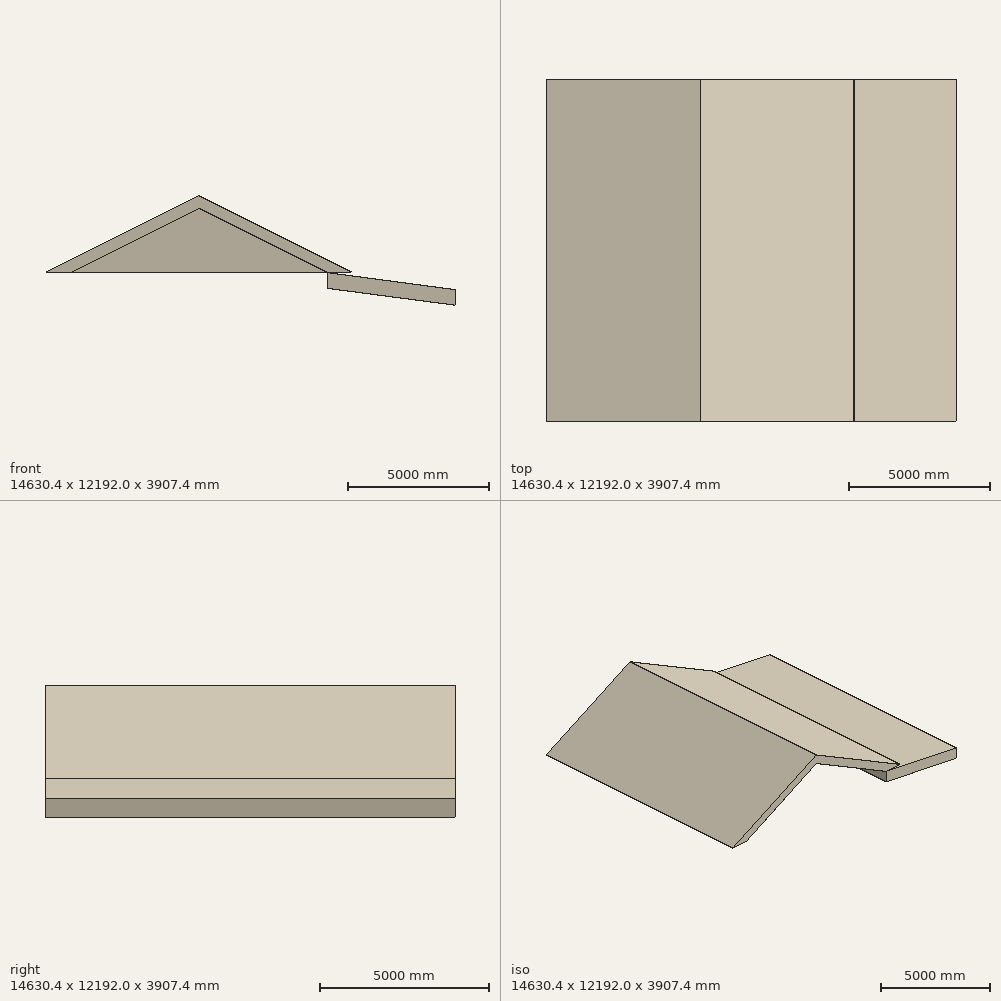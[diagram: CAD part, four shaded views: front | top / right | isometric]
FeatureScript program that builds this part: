
annotation { "Feature Type Name" : "Feature", "Feature Type Description" : "" }
export const myFeature = defineFeature(function(context is Context, id is Id, definition is map)
    precondition{}
    {
        {
            var Q0;
            Q0=qCreatedBy(makeId("Front.planeOp"),FACE);
            var sketch = newSketch(context, id + "F0", { "sketchPlane" : qUnion([Q0])});
            skLineSegment(sketch, "E0", {"start": v(0, 0) * mm, "end": v(-4572, 0) * mm});
            skLineSegment(sketch, "E1", {"start": v(0, 0) * mm, "end": v(4572, 0) * mm});
            skLineSegment(sketch, "E2", {"start": v(0, 0) * mm, "end": v(0, 2286) * mm});
            skLineSegment(sketch, "E3", {"start": v(0, 2286) * mm, "end": v(0, 2743.2) * mm});
            skLineSegment(sketch, "E4", {"start": v(4572, 0) * mm, "end": v(0, 2286) * mm});
            skLineSegment(sketch, "E5", {"start": v(0, 2286) * mm, "end": v(-4572, 0) * mm});
            skLineSegment(sketch, "E6", {"start": v(-4572, 0) * mm, "end": v(-5486.4, 0) * mm});
            skLineSegment(sketch, "E7", {"start": v(4572, 0) * mm, "end": v(5486.4, 0) * mm});
            skLineSegment(sketch, "E8", {"start": v(0, 2743.2) * mm, "end": v(-5486.4, 0) * mm});
            skLineSegment(sketch, "E9", {"start": v(0, 2743.2) * mm, "end": v(5486.4, 0) * mm});
            skLineSegment(sketch, "E10", {"start": v(-4572, 0) * mm, "end": v(-4572, -3352.8) * mm});
            skLineSegment(sketch, "E11", {"start": v(4572, 0) * mm, "end": v(4572, -3352.8) * mm});
            skLineSegment(sketch, "E12", {"start": v(-4572, -3352.8) * mm, "end": v(4572, -3352.8) * mm});
            skLineSegment(sketch, "E13", {"start": v(-4572, -3352.8) * mm, "end": v(-4572, -3962.4) * mm});
            skLineSegment(sketch, "E14", {"start": v(4572, -3352.8) * mm, "end": v(4572, -3962.4) * mm});
            skLineSegment(sketch, "E15", {"start": v(4572, -3962.4) * mm, "end": v(-4572, -3962.4) * mm});
            skLineSegment(sketch, "E16", {"start": v(4572, -3962.4) * mm, "end": v(9144, -3962.4) * mm});
            skLineSegment(sketch, "E17", {"start": v(4572, -3352.8) * mm, "end": v(9144, -3352.8) * mm});
            skLineSegment(sketch, "E18", {"start": v(9144, -3352.8) * mm, "end": v(9144, -609.6) * mm});
            skLineSegment(sketch, "E19", {"start": v(4572, -561) * mm, "end": v(9144, -1164.23) * mm});
            skLineSegment(sketch, "E20", {"start": v(4572, 0) * mm, "end": v(9144, -609.6) * mm});
            skLineSegment(sketch, "E21", {"start": v(-2934.56, -1219.2) * mm, "end": v(-2934.56, -3352.8) * mm});
            skLineSegment(sketch, "E22", {"start": v(-2934.56, -1219.2) * mm, "end": v(-2020.16, -1219.2) * mm});
            skLineSegment(sketch, "E23", {"start": v(-2020.16, -1219.2) * mm, "end": v(-2020.16, -3352.8) * mm});
            skLineSegment(sketch, "E24", {"start": v(-2020.16, -3352.8) * mm, "end": v(-1715.36, -3352.8) * mm});
            skLineSegment(sketch, "E25", {"start": v(-1715.36, -3352.8) * mm, "end": v(-1715.36, -949.84) * mm});
            skLineSegment(sketch, "E26", {"start": v(-1753.41, -949.84) * mm, "end": v(-3239.36, -949.84) * mm});
            skLineSegment(sketch, "E27", {"start": v(-3239.36, -949.84) * mm, "end": v(-3239.36, -3352.8) * mm});
            skLineSegment(sketch, "E28", {"start": v(-3239.36, -3352.8) * mm, "end": v(-2934.56, -3352.8) * mm});
            skLineSegment(sketch, "E29", {"start": v(457.2, -2286) * mm, "end": v(3200.4, -2286) * mm});
            skLineSegment(sketch, "E30", {"start": v(457.2, -914.4) * mm, "end": v(3200.4, -914.4) * mm});
            skLineSegment(sketch, "E31", {"start": v(3200.4, -914.4) * mm, "end": v(3200.4, -2286) * mm});
            skLineSegment(sketch, "E32", {"start": v(457.2, -914.4) * mm, "end": v(457.2, -2286) * mm});
            skLineSegment(sketch, "E33.0", {"start": v(304.8, -762) * mm, "end": v(3352.8, -762) * mm});
            skLineSegment(sketch, "E33.1", {"start": v(304.8, -762) * mm, "end": v(304.8, -2438.4) * mm});
            skLineSegment(sketch, "E33.2", {"start": v(304.8, -2438.4) * mm, "end": v(3352.8, -2438.4) * mm});
            skLineSegment(sketch, "E33.3", {"start": v(3352.8, -762) * mm, "end": v(3352.8, -2438.4) * mm});
            skSolve(sketch);
        }
        {
            var Q0;
            Q0=makeQuery(id+"F0.imprint","IMPRINT",FACE,{"disambiguationData":[TD([[makeQuery(id+"F0.imprint","IMPRINT",EDGE,{"derivedFrom":sQuery(id+"F0.wireOp",EDGE,"E3")}),1.0]])]});
            var Q1;
            Q1=makeQuery(id+"F0.imprint","IMPRINT",FACE,{"disambiguationData":[TD([[makeQuery(id+"F0.imprint","IMPRINT",EDGE,{"derivedFrom":sQuery(id+"F0.wireOp",EDGE,"E3")}),-1.0]])]});
            extrude(context, id + "F1", {"entities" : qUnion([Q0, Q1]), "depth" : 12192 * mm, "offsetDistance" : 30.48 * mm});
        }
        {
            var Q0;
            Q0=makeQuery(id+"F0.imprint","IMPRINT",FACE,{"disambiguationData":[TD([[makeQuery(id+"F0.imprint","IMPRINT",EDGE,{"derivedFrom":sQuery(id+"F0.wireOp",EDGE,"E0")}),-1.0]])]});
            var Q1;
            Q1=makeQuery(id+"F0.imprint","IMPRINT",FACE,{"disambiguationData":[TD([[makeQuery(id+"F0.imprint","IMPRINT",EDGE,{"derivedFrom":sQuery(id+"F0.wireOp",EDGE,"E1")}),1.0]])]});
            extrude(context, id + "F2", {"entities" : qUnion([Q0, Q1]), "operationType" : NewBodyOperationType.ADD, "depth" : 30.48 * mm, "offsetDistance" : 30.48 * mm});
        }
        {
            var Q0;
            {var subQ2=sQuery(id+"F0.wireOp",EDGE,"E19");Q0=makeQuery(id+"F0.imprint","IMPRINT",FACE,{"disambiguationData":[TD([[makeQuery(id+"F0.imprint","IMPRINT",EDGE,{"derivedFrom":subQ2}),1.0]])]});}
            extrude(context, id + "F3", {"entities" : qUnion([Q0]), "depth" : 12192 * mm, "offsetDistance" : 30.48 * mm});
        }
    });
